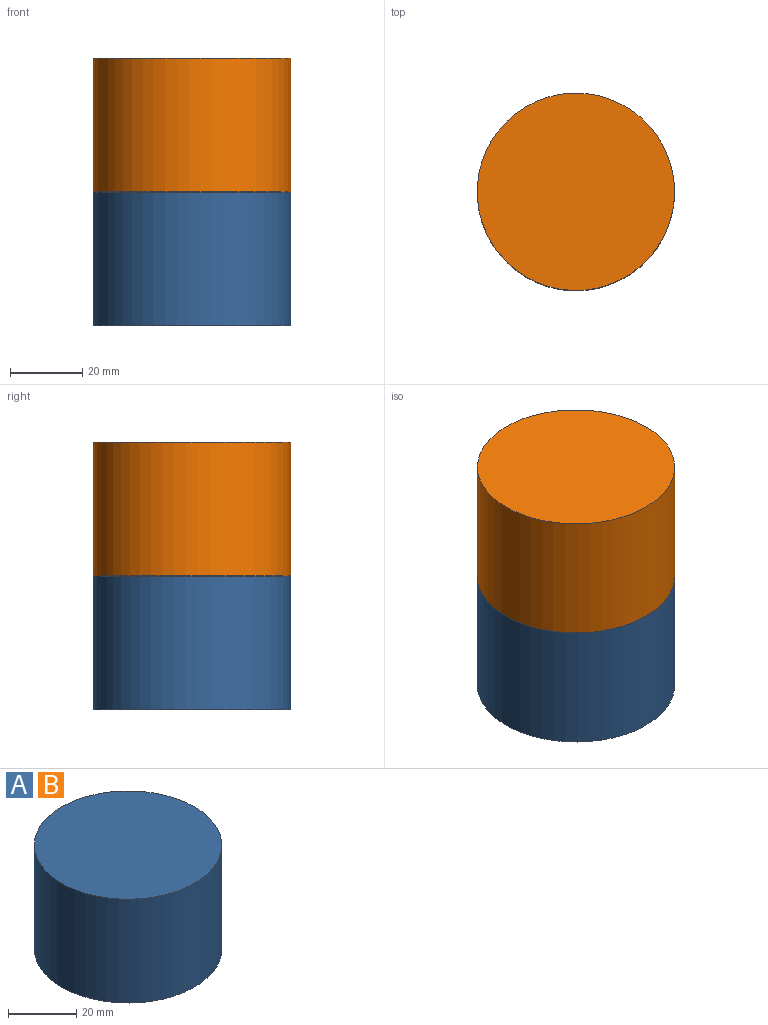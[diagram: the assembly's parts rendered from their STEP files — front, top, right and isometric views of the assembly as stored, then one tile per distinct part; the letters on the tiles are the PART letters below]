
ASSEMBLY  parts=2 mates=1
PART A: 3 faces, bbox 54.8x54.8x37.1 mm
  f0: plane 54.8x54.8mm, normal (0,0,1), area 2358.4mm2, adj f2
  f1: plane 54.8x54.8mm, normal (0,0,-1), area 2358.4mm2, adj f2
  f2: cylinder r=27.4mm len=54.8mm, axis (0,0,1), area 6386mm2, adj f0,f1
PART B: same geometry as A
PLACE A t=(19.79,19.83,-33.26)mm
PLACE B t=(19.79,19.83,3.83)mm
MATE planar B.f2 <-> A.f2  axis (0,0,-1) through (19.79,19.83,-15.9)mm
